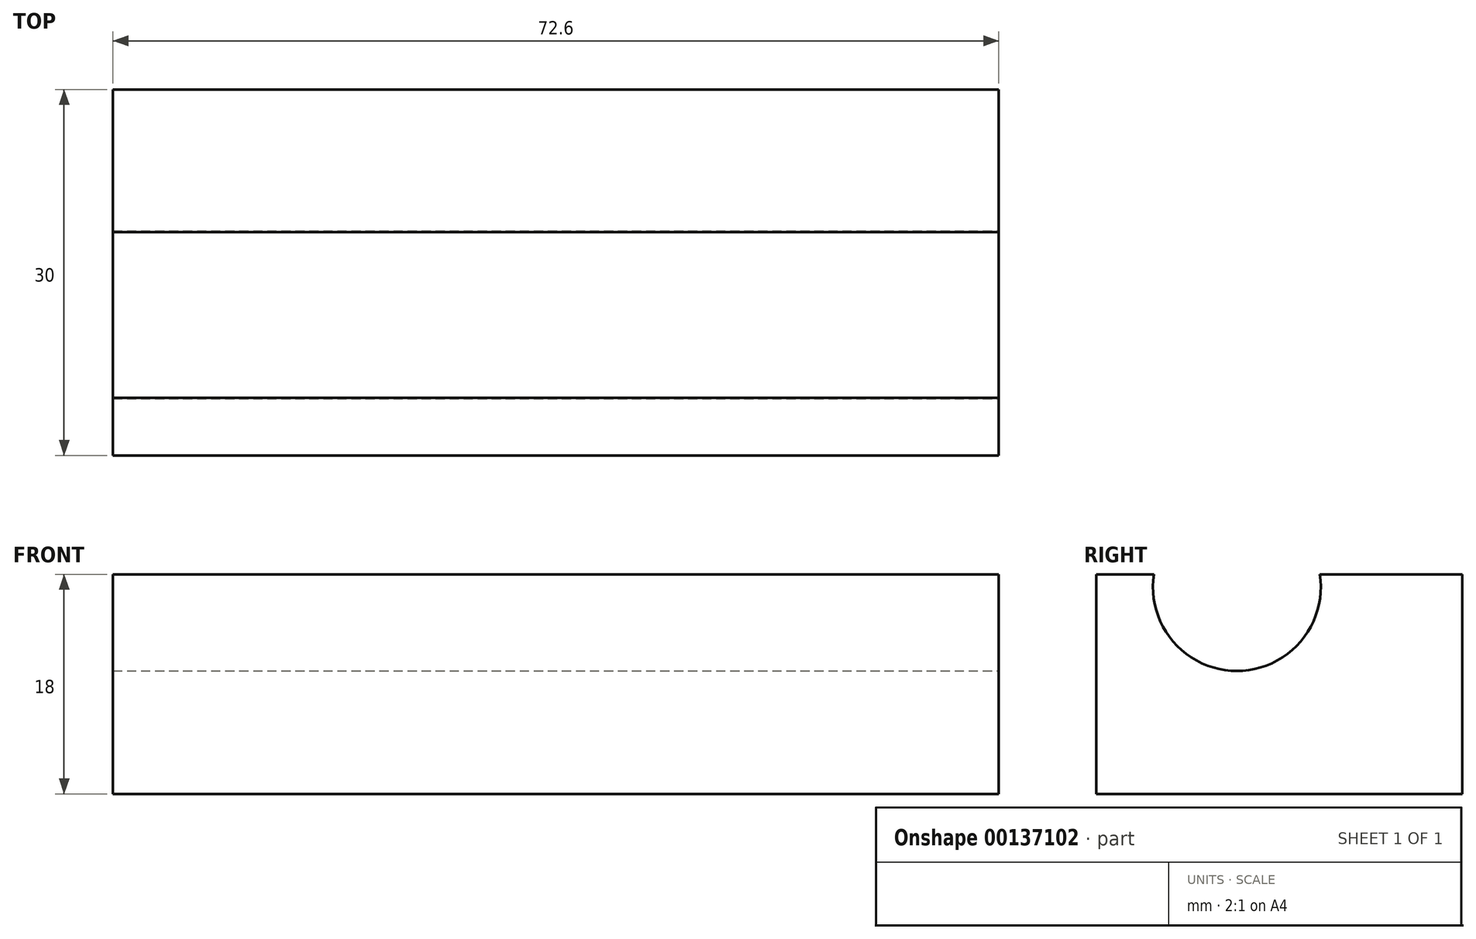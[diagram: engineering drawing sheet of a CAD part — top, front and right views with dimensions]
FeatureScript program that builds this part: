
annotation { "Feature Type Name" : "Feature", "Feature Type Description" : "" }
export const myFeature = defineFeature(function(context is Context, id is Id, definition is map)
    precondition{}
    {
        {
            var Q0;
            Q0=qCreatedBy(makeId("Top.planeOp"),FACE);
            var sketch = newSketch(context, id + "F0", { "sketchPlane" : qUnion([Q0])});
            skLineSegment(sketch, "E0.bottom", {"start": v(-36.3, 15) * mm, "end": v(36.3, 15) * mm});
            skLineSegment(sketch, "E0.top", {"start": v(-36.3, -15) * mm, "end": v(36.3, -15) * mm});
            skLineSegment(sketch, "E0.left", {"start": v(-36.3, 15) * mm, "end": v(-36.3, -15) * mm});
            skLineSegment(sketch, "E0.right", {"start": v(36.3, 15) * mm, "end": v(36.3, -15) * mm});
            skPoint(sketch, "E0.middle", {"position": v(0, 0) * mm});
            skSolve(sketch);
        }
        {
            var Q0;
            Q0 = qSketchRegion(id + "F0", true);
            extrude(context, id + "F1", {"entities" : qUnion([Q0]), "oppositeDirection" : true, "depth" : 18 * mm});
        }
        {
            var Q0;
            Q0=qCreatedBy(makeId("Right.planeOp"),FACE);
            var sketch = newSketch(context, id + "F2", { "sketchPlane" : qUnion([Q0])});
            skCircle(sketch, "E1", {"center": v(-3.47, -1.05) * mm, "radius": 6.88 * mm});
            skSolve(sketch);
        }
        {
            var Q0;
            Q0 = qSketchRegion(id + "F2", true);
            extrude(context, id + "F3", {"entities" : qUnion([Q0]), "operationType" : NewBodyOperationType.REMOVE, "endBound" : BoundingType.THROUGH_ALL, "oppositeDirection" : true, "depth" : 25 * mm, "hasSecondDirection" : true, "secondDirectionOppositeDirection" : false, "secondDirectionDepth" : 45 * mm});
        }
    });
